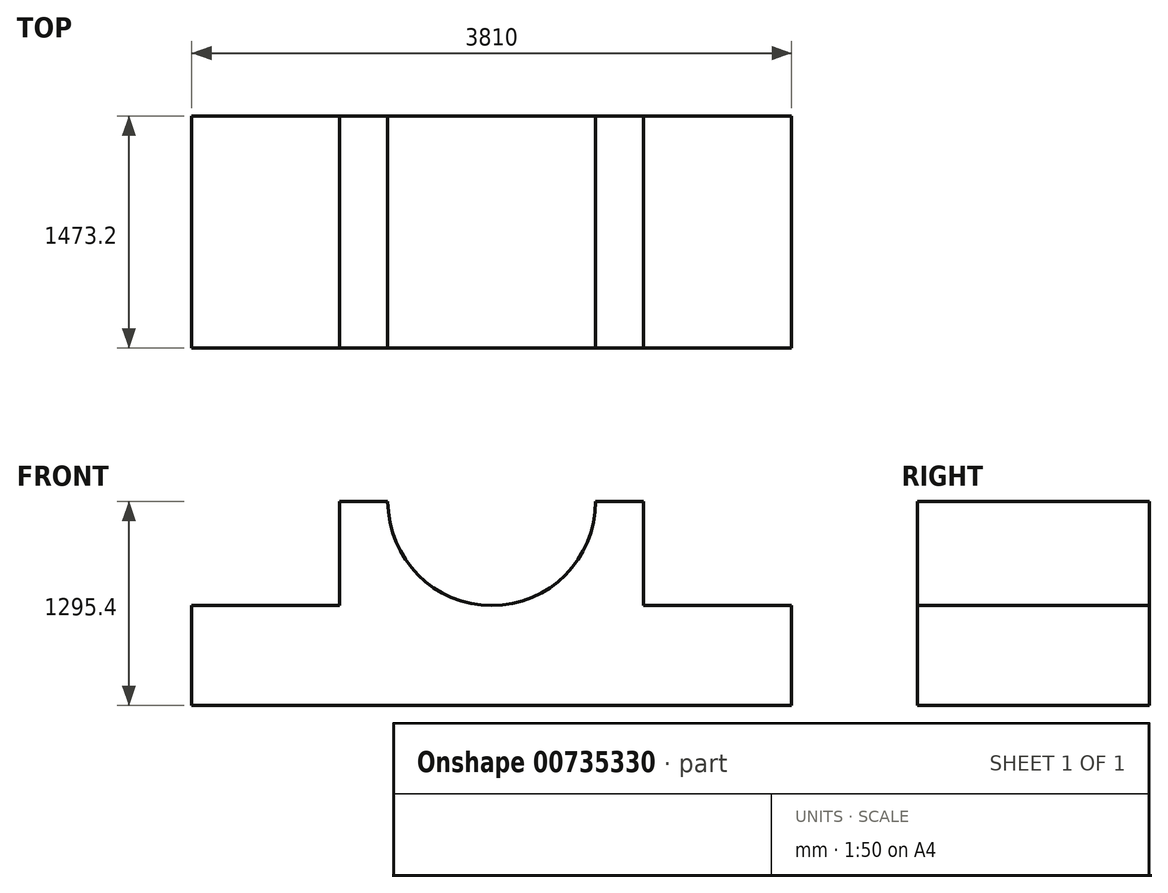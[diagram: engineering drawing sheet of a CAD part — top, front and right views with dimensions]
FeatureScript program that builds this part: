
annotation { "Feature Type Name" : "Feature", "Feature Type Description" : "" }
export const myFeature = defineFeature(function(context is Context, id is Id, definition is map)
    precondition{}
    {
        {
            var Q0;
            Q0=qCreatedBy(makeId("Front.planeOp"),FACE);
            var sketch = newSketch(context, id + "F0", { "sketchPlane" : qUnion([Q0])});
            skLineSegment(sketch, "E0.bottom", {"start": v(-1244.6, 593.72) * mm, "end": v(2565.4, 593.72) * mm});
            skLineSegment(sketch, "E0.top", {"start": v(-1244.6, -41.28) * mm, "end": v(2565.4, -41.28) * mm});
            skLineSegment(sketch, "E0.left", {"start": v(-1244.6, 593.72) * mm, "end": v(-1244.6, -41.28) * mm});
            skLineSegment(sketch, "E0.right", {"start": v(2565.4, 593.72) * mm, "end": v(2565.4, -41.28) * mm});
            skLineSegment(sketch, "E1", {"start": v(-304.8, 593.72) * mm, "end": v(-304.8, 1254.12) * mm});
            skLineSegment(sketch, "E2", {"start": v(1625.6, 593.72) * mm, "end": v(1625.6, 1254.12) * mm});
            skLineSegment(sketch, "E3", {"start": v(-304.8, 1254.12) * mm, "end": v(0, 1254.12) * mm});
            skCircle(sketch, "E4", {"center": v(660.4, 1254.12) * mm, "radius": 660.4 * mm});
            skLineSegment(sketch, "E5", {"start": v(1625.6, 1254.12) * mm, "end": v(1320.8, 1254.12) * mm});
            skSolve(sketch);
        }
        {
            var Q0;
            Q0=makeQuery(id+"F0.imprint","IMPRINT",FACE,{"disambiguationData":[TD([[makeQuery(id+"F0.imprint","IMPRINT",EDGE,{"derivedFrom":sQuery(id+"F0.wireOp",EDGE,"E0.top")}),1.0]])]});
            var Q1;
            {var subQ0=sQuery(id+"F0.wireOp",EDGE,"E2");Q1=makeQuery(id+"F0.imprint","IMPRINT",FACE,{"disambiguationData":[TD([[makeQuery(id+"F0.imprint","IMPRINT",EDGE,{"derivedFrom":subQ0}),1.0]])]});}
            var Q2;
            {var subQ0=sQuery(id+"F0.wireOp",EDGE,"E1");Q2=makeQuery(id+"F0.imprint","IMPRINT",FACE,{"disambiguationData":[TD([[makeQuery(id+"F0.imprint","IMPRINT",EDGE,{"derivedFrom":subQ0}),-1.0]])]});}
            extrude(context, id + "F1", {"entities" : qUnion([Q0, Q1, Q2]), "depth" : 1473.2 * mm, "offsetDistance" : 25.4 * mm});
        }
    });
